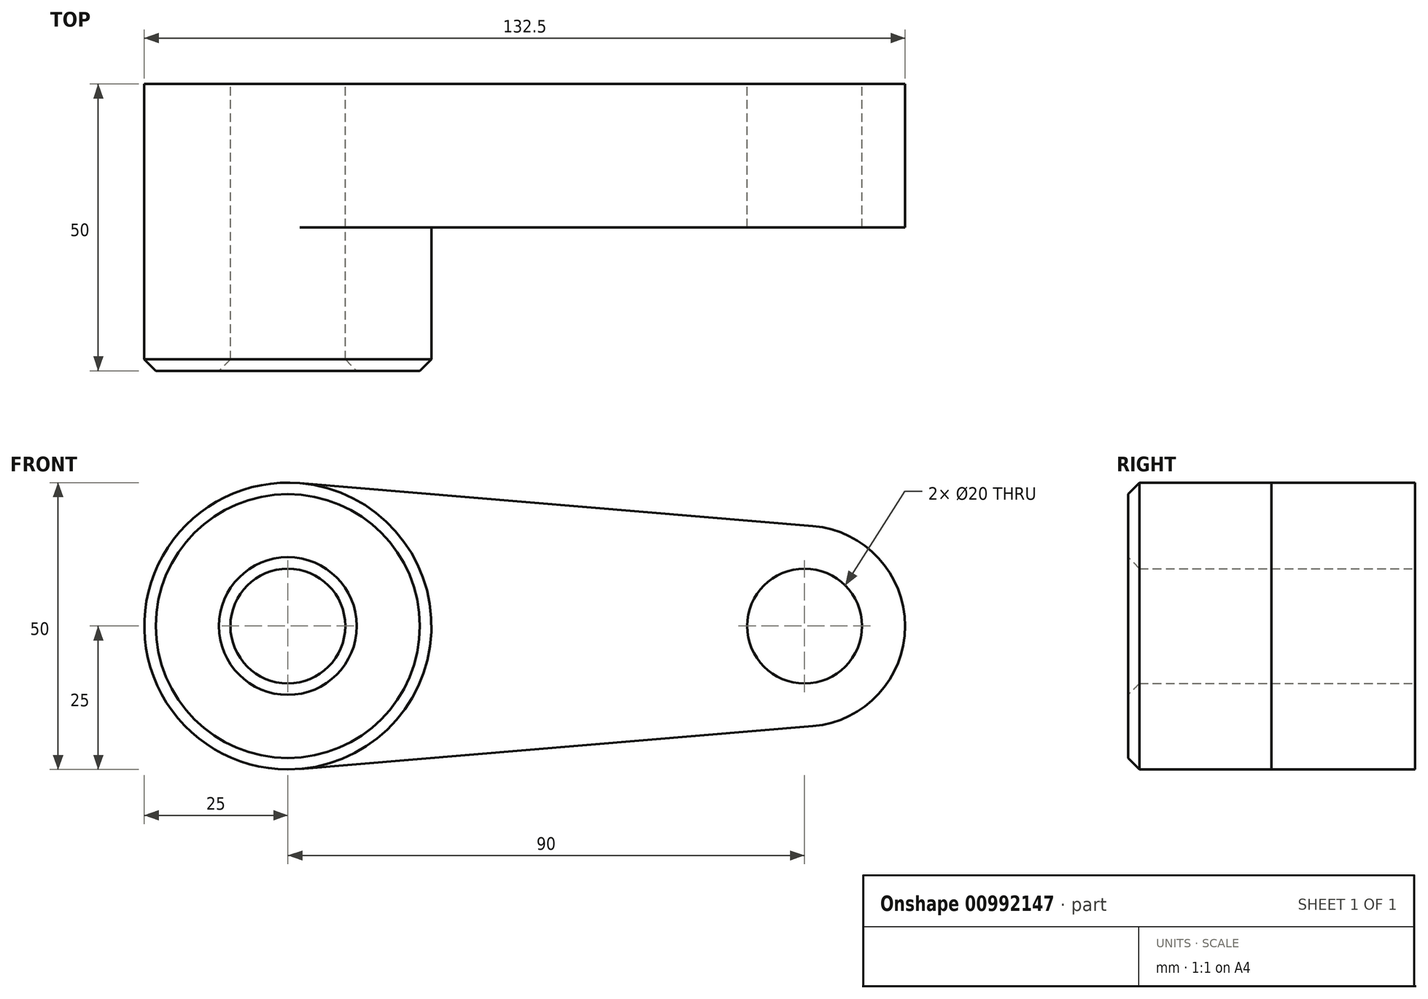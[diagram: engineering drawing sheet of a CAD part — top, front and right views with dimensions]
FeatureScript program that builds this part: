
annotation { "Feature Type Name" : "Feature", "Feature Type Description" : "" }
export const myFeature = defineFeature(function(context is Context, id is Id, definition is map)
    precondition{}
    {
        {
            var Q0;
            Q0=qCreatedBy(makeId("Front.planeOp"),FACE);
            var sketch = newSketch(context, id + "F0", { "sketchPlane" : qUnion([Q0])});
            skCircle(sketch, "E0", {"center": v(0, 0) * mm, "radius": 25 * mm});
            skCircle(sketch, "E1", {"center": v(90, 0) * mm, "radius": 17.5 * mm});
            skLineSegment(sketch, "E2", {"start": v(2.08, 24.91) * mm, "end": v(91.46, 17.44) * mm});
            skLineSegment(sketch, "E3", {"start": v(2.08, -24.91) * mm, "end": v(91.46, -17.44) * mm});
            skCircle(sketch, "E4", {"center": v(0, 0) * mm, "radius": 10 * mm});
            skCircle(sketch, "E5", {"center": v(90, 0) * mm, "radius": 10 * mm});
            skSolve(sketch);
        }
        {
            var Q0;
            Q0=qSketchRegion(id+"F0",true);
            extrude(context, id + "F1", {"entities" : qUnion([Q0]), "depth" : 25 * mm});
        }
        {
            var Q0;
            Q0=makeQuery(id+"F0.imprint","IMPRINT",FACE,{"disambiguationData":[TD([[makeQuery(id+"F0.imprint","IMPRINT",EDGE,{"derivedFrom":sQuery(id+"F0.wireOp",EDGE,"E4")}),-1.0]])]});
            extrude(context, id + "F2", {"entities" : qUnion([Q0]), "operationType" : NewBodyOperationType.ADD, "depth" : 50 * mm});
        }
        {
            var Q0;
            Q0=makeQuery(id+"F2.opExtrude","CAP_EDGE",EDGE,{"disambiguationData":[OSD([sQuery(id+"F0.wireOp",EDGE,"E0")])],"isStart":false});
            var Q1;
            Q1=makeQuery(id+"F2.opExtrude","CAP_EDGE",EDGE,{"disambiguationData":[OSD([sQuery(id+"F0.wireOp",EDGE,"E4")])],"isStart":false});
            var Q2;
            Q2=makeQuery(id+"F1.opExtrude","CAP_EDGE",EDGE,{"disambiguationData":[OSD([sQuery(id+"F0.wireOp",EDGE,"E5")])],"isStart":false});
            chamfer(context, id + "F3", {"entities" : qUnion([Q0, Q1, Q2]), "width" : 2 * mm, "tangentPropagation" : true});
        }
        {
            var Q0;
            Q0=qCreatedBy(makeId("Front.planeOp"),FACE);
            var sketch = newSketch(context, id + "F4", { "sketchPlane" : qUnion([Q0])});
            skCircle(sketch, "E6", {"center": v(26.63, 23.54) * mm, "radius": 29.82 * mm});
            skSolve(sketch);
        }
        {
            var Q0;
            Q0=makeQuery(id+"F4.imprint","IMPRINT",FACE,{"disambiguationData":[TD([[makeQuery(id+"F4.imprint","IMPRINT",EDGE,{"derivedFrom":sQuery(id+"F4.wireOp",EDGE,"E6")}),1.0]])]});
            var sketch = newSketch(context, id + "F5", { "sketchPlane" : qUnion([Q0])});
            skSolve(sketch);
        }
        {
            var Q0;
            Q0=makeQuery(id+"F0.imprint","IMPRINT",FACE,{"disambiguationData":[TD([[makeQuery(id+"F0.imprint","IMPRINT",EDGE,{"derivedFrom":sQuery(id+"F0.wireOp",EDGE,"E4")}),-1.0]])]});
            var Q1;
            Q1=makeQuery(id+"F5.imprint","IMPRINT",FACE,{"disambiguationData":[TD([[makeQuery(id+"F5.imprint","IMPRINT",EDGE,{"derivedFrom":makeQuery(id+"F4.imprint","IMPRINT",EDGE,{"derivedFrom":sQuery(id+"F4.wireOp",EDGE,"E6")})}),1.0]])]});
            var Q2;
            Q2 = qSketchRegion(id + "F0", true);
            var Q3;
            {var subQ0=sQuery(id+"F0.wireOp",EDGE,"E2");Q3=makeQuery(id+"F0.imprint","IMPRINT",FACE,{"disambiguationData":[TD([[makeQuery(id+"F0.imprint","IMPRINT",EDGE,{"derivedFrom":subQ0}),-1.0]])]});}
            extrude(context, id + "F6", {"entities" : qUnion([Q0, Q1, Q2, Q3]), "operationType" : NewBodyOperationType.ADD, "depth" : 25 * mm, "offsetDistance" : 25 * mm});
        }
    });
